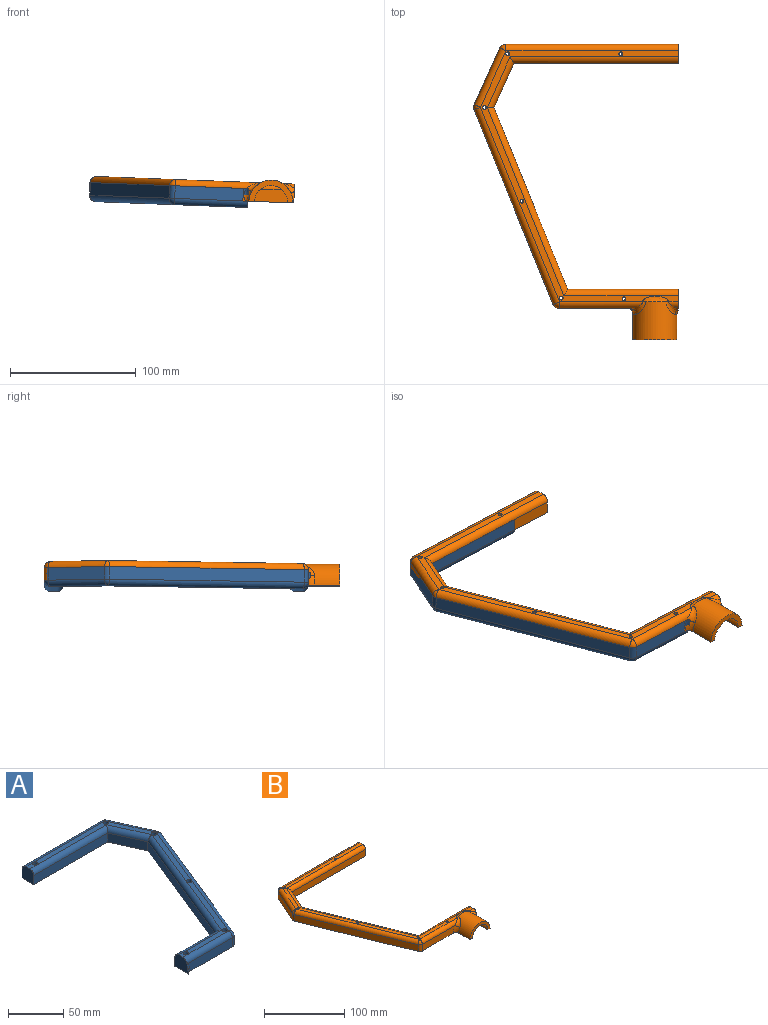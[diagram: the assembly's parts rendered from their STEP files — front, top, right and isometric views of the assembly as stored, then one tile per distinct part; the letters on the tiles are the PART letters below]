
ASSEMBLY  parts=2 mates=1
PART A: 50 faces, bbox 131.7x216.2x16.2 mm
  f0: plane 9.39x5mm, normal (0,0,1), area 37.1mm2, adj f22,f24,f37,f40
  f1: plane 1.82x0.79mm, normal (0,0,1), area 0.3mm2, adj f22,f23,f42
  f2: plane 83.92x81.12mm, normal (0,0,1), area 630.2mm2, adj f12,f21,f26,f27,f38,f46,f48
  f3: plane 6.49x5mm, normal (0,0,1), area 22.6mm2, adj f12,f27,f36,f38
  f4: cylinder r=1.5mm len=10mm, axis (0,0,-1), area 94.2mm2, adj f10,f49
  f5: cylinder r=1.5mm len=10mm, axis (0,0,-1), area 94.2mm2, adj f10,f47
  f6: cylinder r=1.5mm len=10mm, axis (0,0,-1), area 94.2mm2, adj f10,f45
  f7: cylinder r=1.5mm len=10mm, axis (0,0,-1), area 94.2mm2, adj f10,f43
  f8: cylinder r=1.5mm len=10mm, axis (0,0,-1), area 94.2mm2, adj f10,f41
  f9: cylinder r=1.5mm len=10mm, axis (0,0,-1), area 94.2mm2, adj f10,f39
  f10: plane 212.12x126.15mm, normal (0,0,-1), area 5460.6mm2, adj f4,f5,f6,f7,f8,f9,f11,f13
  f11: plane 56.48x10mm, normal (0,-1,0), area 549mm2, adj f10,f12,f28,f35
  f12: cylinder r=5mm len=58.22mm, axis (-1,0,0), area 456mm2, adj f2,f3,f11,f29,f34,f36
  f13: plane 154.9x62.93mm, normal (0.93,-0.38,0), area 1671.9mm2, adj f10,f21,f28,f30
  f14: plane 45.1x20.3mm, normal (0.91,0.41,0), area 494.6mm2, adj f10,f23,f30,f32
  f15: plane 94.39x10mm, normal (0,-1,0), area 943.9mm2, adj f10,f16,f24,f37
  f16: plane 35.3x15.89mm, normal (-0.91,-0.41,0), area 387.1mm2, adj f10,f15,f17,f25
  f17: plane 144.7x58.78mm, normal (-0.93,0.38,0), area 1561.8mm2, adj f10,f16,f18,f26
  f18: plane 51.49x10mm, normal (0,1,0), area 514.9mm2, adj f10,f17,f27,f36
  f19: plane 100.85x10mm, normal (0,1,0), area 1008.5mm2, adj f10,f22,f32,f37
  f20: plane 120.76x111.76mm, normal (0,0,1), area 1027.4mm2, adj f21,f22,f23,f24,f25,f26,f40,f42
  f21: cylinder r=5mm len=156.78mm, axis (-0.38,-0.93,0), area 1313.1mm2, adj f2,f13,f20,f29,f31
  f22: cylinder r=5mm len=100.85mm, axis (1,0,0), area 792.1mm2, adj f0,f1,f19,f20,f33,f37
  f23: cylinder r=5mm len=47.15mm, axis (0.41,-0.91,0), area 388.3mm2, adj f1,f14,f20,f31,f33,f42
  f24: cylinder r=5mm len=97.62mm, axis (-1,0,0), area 754mm2, adj f0,f15,f20,f25,f37
  f25: cylinder r=5mm len=42.1mm, axis (-0.41,0.91,0), area 319.2mm2, adj f16,f20,f24,f26,f44
  f26: cylinder r=5mm len=151.52mm, axis (0.38,0.93,0), area 1242.2mm2, adj f2,f17,f20,f25,f27,f44
  f27: cylinder r=5mm len=54.86mm, axis (1,0,0), area 417.6mm2, adj f2,f3,f18,f26,f36
  f28: cylinder r=5mm len=10mm, axis (0,0,-1), area 59.2mm2, adj f10,f11,f13,f29
  f29: sphere r=5mm, area 29.6mm2, adj f12,f21,f28
  f30: cylinder r=5mm len=10mm, axis (0,0,-1), area 40.4mm2, adj f10,f13,f14,f31
  f31: sphere r=5mm, area 20.2mm2, adj f21,f23,f30
  f32: cylinder r=5mm len=10mm, axis (0,0,-1), area 57.4mm2, adj f10,f14,f19,f33
  f33: sphere r=5mm, area 32.5mm2, adj f22,f23,f32
  f34: bspline ~7.05x5.56mm, area 2mm2, adj f12,f35,f36
  f35: torus R=22.5mm, axis (0,1,0), area 32.5mm2, adj f10,f11,f34,f36
  f36: plane 18.3x16.18mm, normal (-1,0,0), area 227.4mm2, adj f3,f10,f12,f18,f27,f34,f35
  f37: plane 15x15mm, normal (-1,0,0), area 214.3mm2, adj f0,f10,f15,f19,f22,f24
  f38: cylinder r=2.5mm len=5mm, axis (0,0,1), area 78.5mm2, adj f2,f3,f39
  f39: plane 5x5mm, normal (0,0,1), area 12.6mm2, adj f9,f38
  f40: cylinder r=2.5mm len=5mm, axis (0,0,1), area 78.5mm2, adj f0,f20,f41
  f41: plane 5x5mm, normal (0,0,1), area 12.6mm2, adj f8,f40
  f42: cylinder r=2.5mm len=5mm, axis (0,0,1), area 78.5mm2, adj f1,f20,f23,f43
  f43: plane 5x5mm, normal (0,0,1), area 12.6mm2, adj f7,f42
  f44: cylinder r=2.5mm len=5mm, axis (0,0,1), area 78.5mm2, adj f20,f25,f26,f45
  f45: plane 5x5mm, normal (0,0,1), area 12.6mm2, adj f6,f44
  f46: cylinder r=2.5mm len=5mm, axis (0,0,1), area 78.5mm2, adj f2,f20,f47
  f47: plane 5x5mm, normal (0,0,1), area 12.6mm2, adj f5,f46
  f48: cylinder r=2.5mm len=5mm, axis (0,0,1), area 78.5mm2, adj f2,f49
  f49: plane 5x5mm, normal (0,0,1), area 12.6mm2, adj f4,f48
PART B: 43 faces, bbox 188.9x255x37.5 mm
  f0: plane 235x162.77mm, normal (0,0,-1), area 6779.3mm2, adj f1,f4,f5,f6,f7,f8,f9,f10
  f1: plane 46.4x30mm, normal (0,-1,0), area 235.9mm2, adj f0,f14,f27
  f2: cylinder r=5mm len=7.9mm, axis (-1,0,0), area 24.6mm2, adj f12,f33,f35
  f3: cylinder r=5mm len=66.33mm, axis (-1,0,0), area 482.3mm2, adj f6,f12,f26,f31
  f4: plane 45.1x20.3mm, normal (-0.91,0.41,0), area 494.6mm2, adj f0,f15,f21,f23
  f5: plane 154.9x62.93mm, normal (-0.93,-0.38,0), area 1671.9mm2, adj f0,f13,f23,f25
  f6: plane 56.48x10mm, normal (0,-1,0), area 549mm2, adj f0,f3,f25,f30
  f7: plane 144.7x58.78mm, normal (0.93,0.38,0), area 1561.8mm2, adj f0,f8,f10,f19
  f8: plane 35.3x15.89mm, normal (0.91,-0.41,0), area 387.1mm2, adj f0,f7,f9,f18
  f9: plane 131.01x10mm, normal (0,-1,0), area 1310.1mm2, adj f0,f8,f17,f36
  f10: plane 88.11x10mm, normal (0,1,0), area 881.1mm2, adj f0,f7,f20,f35
  f11: plane 137.48x10mm, normal (0,1,0), area 1374.8mm2, adj f0,f16,f21,f36
  f12: plane 200x157.77mm, normal (0,0,1), area 2086.3mm2, adj f2,f3,f13,f15,f16,f17,f18,f19
  f13: cylinder r=5mm len=156.78mm, axis (-0.38,0.93,0), area 1313.1mm2, adj f5,f12,f24,f26
  f14: cylinder r=5mm len=17.23mm, axis (-1,0,0), area 0mm2, adj f1,f27
  f15: cylinder r=5mm len=47.15mm, axis (0.41,0.91,0), area 388.4mm2, adj f4,f12,f22,f24
  f16: cylinder r=5mm len=137.48mm, axis (1,0,0), area 1079.7mm2, adj f11,f12,f22,f36
  f17: cylinder r=5mm len=134.24mm, axis (-1,0,0), area 1041.7mm2, adj f9,f12,f18,f36
  f18: cylinder r=5mm len=42.25mm, axis (-0.41,-0.91,0), area 325.1mm2, adj f8,f12,f17,f19
  f19: cylinder r=5mm len=151.68mm, axis (0.38,-0.93,0), area 1248.3mm2, adj f7,f12,f18,f20
  f20: cylinder r=5mm len=91.48mm, axis (1,0,0), area 705.3mm2, adj f10,f12,f19,f35
  f21: cylinder r=5mm len=10mm, axis (0,0,-1), area 57.4mm2, adj f0,f4,f11,f22
  f22: sphere r=5mm, area 28.7mm2, adj f15,f16,f21
  f23: cylinder r=5mm len=10mm, axis (0,0,-1), area 40.4mm2, adj f0,f4,f5,f24
  f24: sphere r=5mm, area 20.2mm2, adj f13,f15,f23
  f25: cylinder r=5mm len=10mm, axis (0,0,-1), area 59.2mm2, adj f0,f5,f6,f26
  f26: sphere r=5mm, area 29.6mm2, adj f3,f13,f25
  f27: cylinder r=13.2mm len=26.4mm, axis (0,1,0), area 1036.7mm2, adj f0,f1,f14,f29
  f28: cylinder r=17.5mm len=35mm, axis (0,1,0), area 1377.1mm2, adj f0,f29,f30,f31,f32,f33,f34
  f29: plane 35x17.5mm, normal (0,-1,0), area 207.4mm2, adj f0,f27,f28
  f30: torus R=22.5mm, axis (0,1,0), area 69.9mm2, adj f0,f6,f28,f31
  f31: bspline ~13.03x11.16mm, area 67.2mm2, adj f3,f28,f30,f32
  f32: bspline ~20.62x4.33mm, area 82.3mm2, adj f12,f28,f31,f33
  f33: bspline ~13.03x10.22mm, area 64.8mm2, adj f2,f28,f32,f34,f35
  f34: torus R=22.5mm, axis (0,1,0), area 34.6mm2, adj f0,f28,f33,f35
  f35: plane 18.62x16.18mm, normal (1,0,0), area 229.3mm2, adj f0,f2,f10,f12,f20,f33,f34
  f36: plane 15x15mm, normal (1,0,0), area 214.3mm2, adj f0,f9,f11,f12,f16,f17
  f37: cylinder r=1.5mm len=15mm, axis (0,0,1), area 141.4mm2, adj f0,f12
  f38: cylinder r=1.5mm len=15mm, axis (0,0,1), area 141.4mm2, adj f0,f12
  f39: cylinder r=1.5mm len=15mm, axis (0,0,1), area 141.4mm2, adj f0,f12
  f40: cylinder r=1.5mm len=15mm, axis (0,0,1), area 141.4mm2, adj f0,f12
  f41: cylinder r=1.5mm len=15mm, axis (0,0,1), area 141.4mm2, adj f0,f12
  f42: cylinder r=1.5mm len=15mm, axis (0,0,1), area 141.4mm2, adj f0,f12
PLACE A rot(axis=(0,-1,0),177.8deg) t=(-5.42,5.53,-38.18)mm
PLACE B rot(axis=(0,1,0),2.2deg) t=(-5.8,5.53,-48.17)mm
MATE fastened B.f8 <-> A.f16  axis (0.91,-0.41,-0.03) through (-126.27,97.7,-38.56)mm
